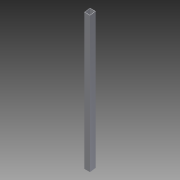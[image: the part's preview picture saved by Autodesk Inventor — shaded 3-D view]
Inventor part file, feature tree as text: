
AUTODESK INVENTOR PART (.ipt)
format: ipt  version: 2013 (Build 170138000, 138)  size: 88,576 bytes
history: native  units: in
note: dims shown in document units (in); Inventor stores cm internally (conversion verified against a paired STEP export)
features: extrude x2, sketch x2
ambient origin geometry x8: Origin, YZ Plane, XZ Plane, XY Plane, X Axis, Y Axis, Z Axis, Center Point
bodies: Solid1 (feature_tree)
feature tree (4):
  extrude  "Extrusion1"  Depth=1.0in
  extrude  "Extrusion2"  Depth=30.0in TaperAngle=0.0deg
  sketch  "Sketch1"  dims[d0=1.0in d2=1.0in]
  sketch  "Sketch2"  dims[d3=0.0625in d4=30.0in d5=0.0in d6=23.5in d8=23.7592in d9=30.0in d10=0.0in]
